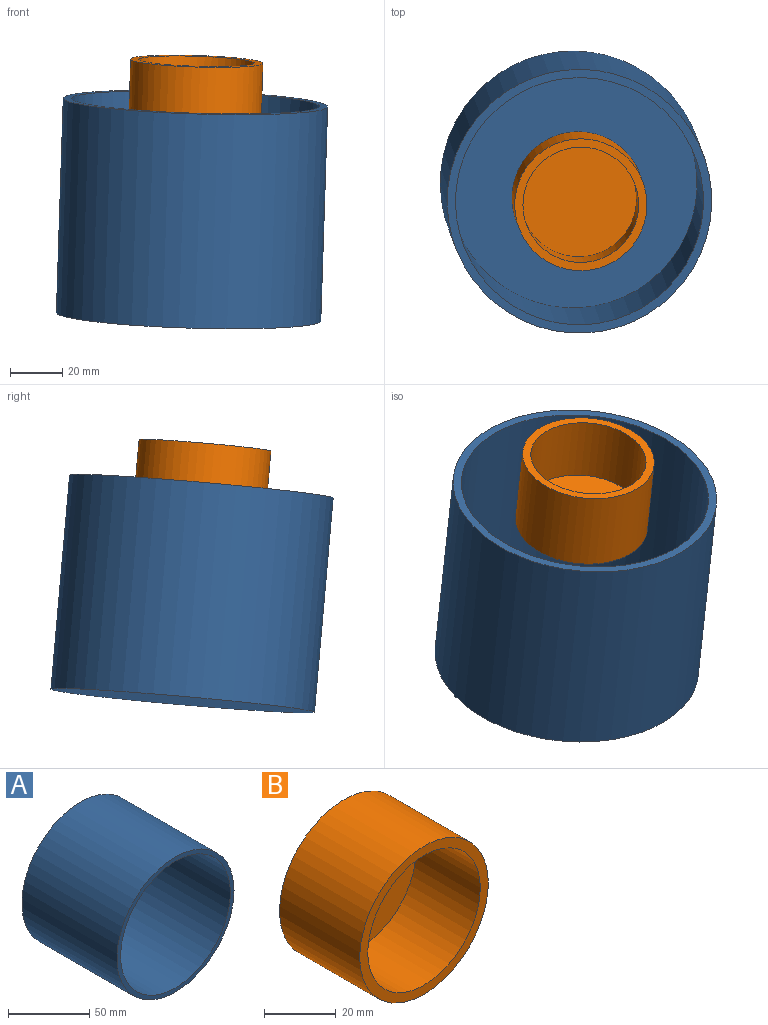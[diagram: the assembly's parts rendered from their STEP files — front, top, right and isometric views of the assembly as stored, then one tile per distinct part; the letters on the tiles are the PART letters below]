
ASSEMBLY  parts=2 mates=1
PART A: 5 faces, bbox 101.6x82.6x101.6 mm
  f0: cylinder r=50.8mm len=101.6mm, axis (0,1,0), area 26348.8mm2, adj f1,f2
  f1: plane 101.6x101.6mm, normal (0,-1,0), area 981.7mm2, adj f0,f3
  f2: plane 101.6x101.6mm, normal (0,1,0), area 8107.3mm2, adj f0
  f3: cylinder r=47.62mm len=95.25mm, axis (0,-1,0), area 22801.8mm2, adj f1,f4
  f4: plane 95.25x95.25mm, normal (0,-1,0), area 7125.6mm2, adj f3
PART B: 5 faces, bbox 50.8x31.8x50.8 mm
  f0: cylinder r=25.4mm len=50.8mm, axis (0,1,0), area 5067.1mm2, adj f1,f2
  f1: plane 50.8x50.8mm, normal (0,-1,0), area 475mm2, adj f0,f3
  f2: plane 50.8x50.8mm, normal (0,1,0), area 2026.8mm2, adj f0
  f3: cylinder r=22.23mm len=44.45mm, axis (0,-1,0), area 3547mm2, adj f1,f4
  f4: plane 44.45x44.45mm, normal (0,-1,0), area 1551.8mm2, adj f3
PLACE A rot(axis=(-1,0.04,0),85.1deg) t=(-38.43,-88.34,-59.41)mm
PLACE B rot(axis=(-1,0.04,0),85.1deg) t=(-107.24,-48.93,13.2)mm
MATE slider B.f0 <-> A.f0  axis (-0.03,0.09,-1) through (-77.42,-83.66,25.16)mm
